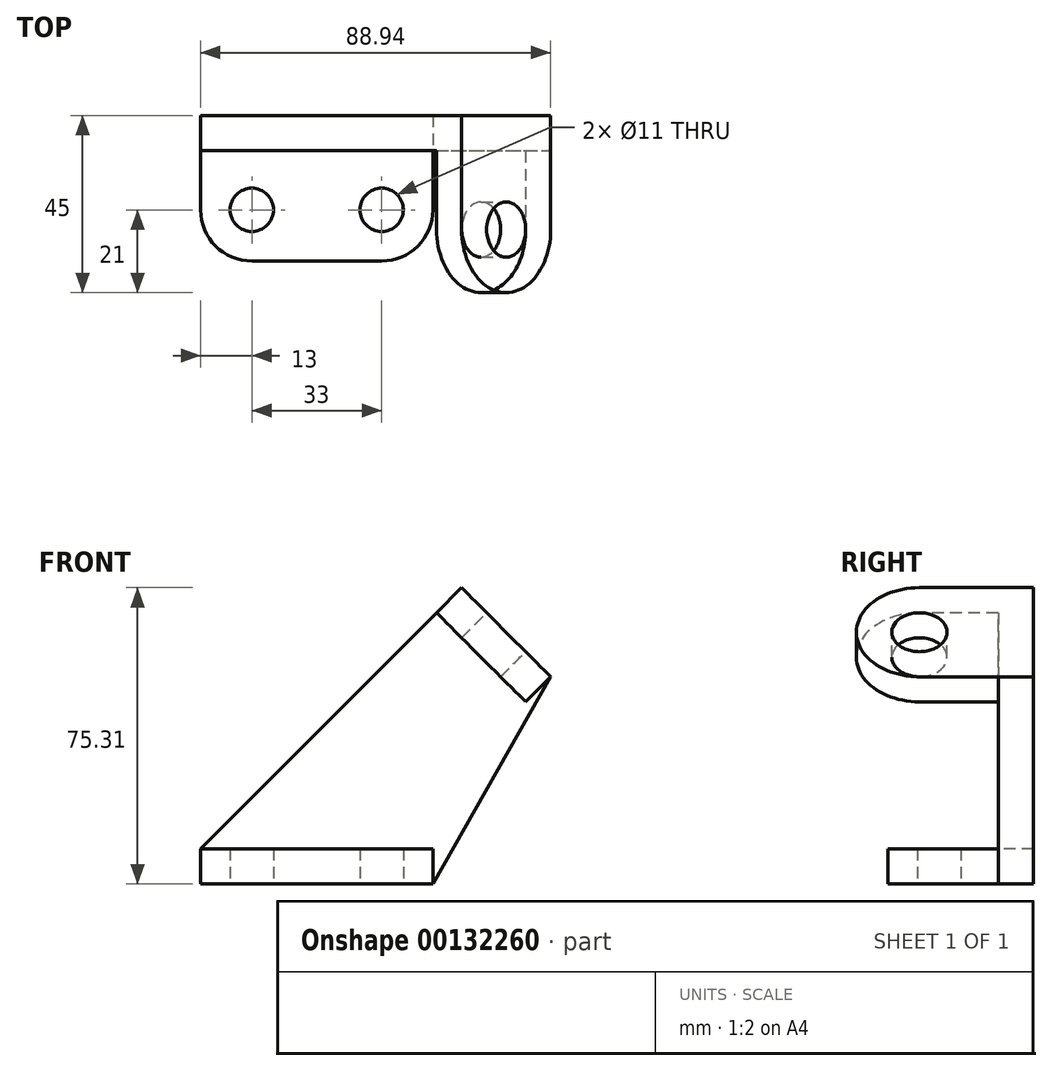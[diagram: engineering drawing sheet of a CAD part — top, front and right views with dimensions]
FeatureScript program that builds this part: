
annotation { "Feature Type Name" : "Feature", "Feature Type Description" : "" }
export const myFeature = defineFeature(function(context is Context, id is Id, definition is map)
    precondition{}
    {
        {
            var Q0;
            Q0=qCreatedBy(makeId("Top.planeOp"),FACE);
            var sketch = newSketch(context, id + "F0", { "sketchPlane" : qUnion([Q0])});
            skCircle(sketch, "E0", {"center": v(0, 0) * mm, "radius": 5.5 * mm});
            skCircle(sketch, "E1", {"center": v(33, 0) * mm, "radius": 5.5 * mm});
            skLineSegment(sketch, "E2.bottom", {"start": v(0, -13) * mm, "end": v(33, -13) * mm});
            skLineSegment(sketch, "E2.top", {"start": v(-13, 15) * mm, "end": v(46, 15) * mm});
            skLineSegment(sketch, "E2.left", {"start": v(-13, 0) * mm, "end": v(-13, 15) * mm});
            skLineSegment(sketch, "E2.right", {"start": v(46, 0) * mm, "end": v(46, 15) * mm});
            skPoint(sketch, "E3.visualSharp", {"position": v(-13, -13) * mm});
            skArc(sketch, "E3.filletArc", {"start": v(-13, 0) * mm, "mid": v(-9.2, -9.2) * mm, "end": v(0, -13) * mm});
            skPoint(sketch, "E4.visualSharp", {"position": v(46, -13) * mm});
            skArc(sketch, "E4.filletArc", {"start": v(33, -13) * mm, "mid": v(42.2, -9.2) * mm, "end": v(46, 0) * mm});
            skSolve(sketch);
        }
        {
            var Q0;
            Q0 = qSketchRegion(id + "F0", true);
            extrude(context, id + "F1", {"entities" : qUnion([Q0]), "depth" : 9 * mm});
        }
        {
            var Q0;
            Q0=makeQuery(id+"F1.opExtrude","SWEPT_FACE",FACE,{"disambiguationData":[OSD([sQuery(id+"F0.wireOp",EDGE,"E2.top")])]});
            var sketch = newSketch(context, id + "F2", { "sketchPlane" : qUnion([Q0])});
            skLineSegment(sketch, "E5", {"start": v(13, 0) * mm, "end": v(13, 9) * mm});
            skLineSegment(sketch, "E6", {"start": v(13, 9) * mm, "end": v(-53.31, 75.31) * mm});
            skLineSegment(sketch, "E7", {"start": v(-46, 0) * mm, "end": v(-75.94, 52.69) * mm});
            skLineSegment(sketch, "E8", {"start": v(-46, 0) * mm, "end": v(13, 0) * mm});
            skLineSegment(sketch, "E9", {"start": v(-53.31, 75.31) * mm, "end": v(-75.94, 52.69) * mm});
            skLineSegment(sketch, "E10", {"start": v(-49.77, 64) * mm, "end": v(-64.63, 64) * mm, "construction": true});
            skSolve(sketch);
        }
        {
            var Q0;
            Q0 = qSketchRegion(id + "F2", true);
            extrude(context, id + "F3", {"entities" : qUnion([Q0]), "operationType" : NewBodyOperationType.ADD, "depth" : 9 * mm});
        }
        {
            var Q0;
            Q0=makeQuery(id+"F3.opExtrude","SWEPT_FACE",FACE,{"disambiguationData":[OSD([sQuery(id+"F2.wireOp",EDGE,"E9")])]});
            var sketch = newSketch(context, id + "F4", { "sketchPlane" : qUnion([Q0])});
            skLineSegment(sketch, "E11", {"start": v(24, -0.44) * mm, "end": v(-5, -0.44) * mm, "construction": true});
            skLineSegment(sketch, "E12", {"start": v(15, 15.56) * mm, "end": v(-5, 15.56) * mm});
            skLineSegment(sketch, "E13", {"start": v(15, 15.56) * mm, "end": v(15, -16.44) * mm});
            skLineSegment(sketch, "E14", {"start": v(15, -16.44) * mm, "end": v(-5, -16.44) * mm});
            skArc(sketch, "E15", {"start": v(-5, 15.56) * mm, "mid": v(-21, -0.44) * mm, "end": v(-5, -16.44) * mm});
            skCircle(sketch, "E16", {"center": v(-5, -0.44) * mm, "radius": 7 * mm});
            skSolve(sketch);
        }
        {
            var Q0;
            Q0 = qSketchRegion(id + "F4", true);
            extrude(context, id + "F5", {"entities" : qUnion([Q0]), "operationType" : NewBodyOperationType.ADD, "oppositeDirection" : true, "depth" : 9 * mm});
        }
    });
